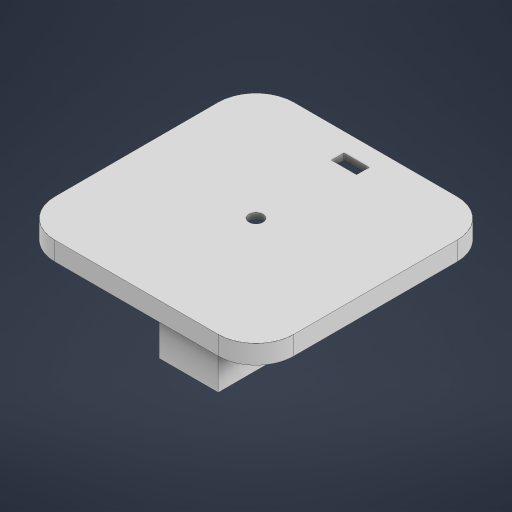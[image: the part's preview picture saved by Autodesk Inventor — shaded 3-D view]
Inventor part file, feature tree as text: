
AUTODESK INVENTOR PART (.ipt)
format: ipt  version: 2024 (Build 280153000, 153)  size: 440,320 bytes
history: native  units: mm
features: extrude x7, sketch x7, other x1, shell x1, projected_geometry x1
ambient origin geometry x8: Origin, YZ Plane, XZ Plane, XY Plane, X Axis, Y Axis, Z Axis, Center Point
bodies: Body1 (feature_tree)
feature tree (17):
  other  "솔리드1"
  extrude  "돌출1"  Depth=190.0mm
  shell  "쉘1"  Thickness=190.0mm
  extrude  "돌출3"  Depth=30.0mm
  extrude  "돌출4"  Depth=15.0mm TaperAngle=0.0deg
  extrude  "돌출5"  Depth=5.0mm
  extrude  "돌출6"  Depth=11.0mm
  extrude  "돌출7"  Depth=95.0mm
  extrude  "돌출8"  Depth=95.0mm
  sketch  "스케치1"
  sketch  "스케치3"
  sketch  "스케치4"
  sketch  "스케치5"
  sketch  "스케치6"
  sketch  "스케치7"
  projected_geometry  "투영된 루프1"
  sketch  "스케치8"
